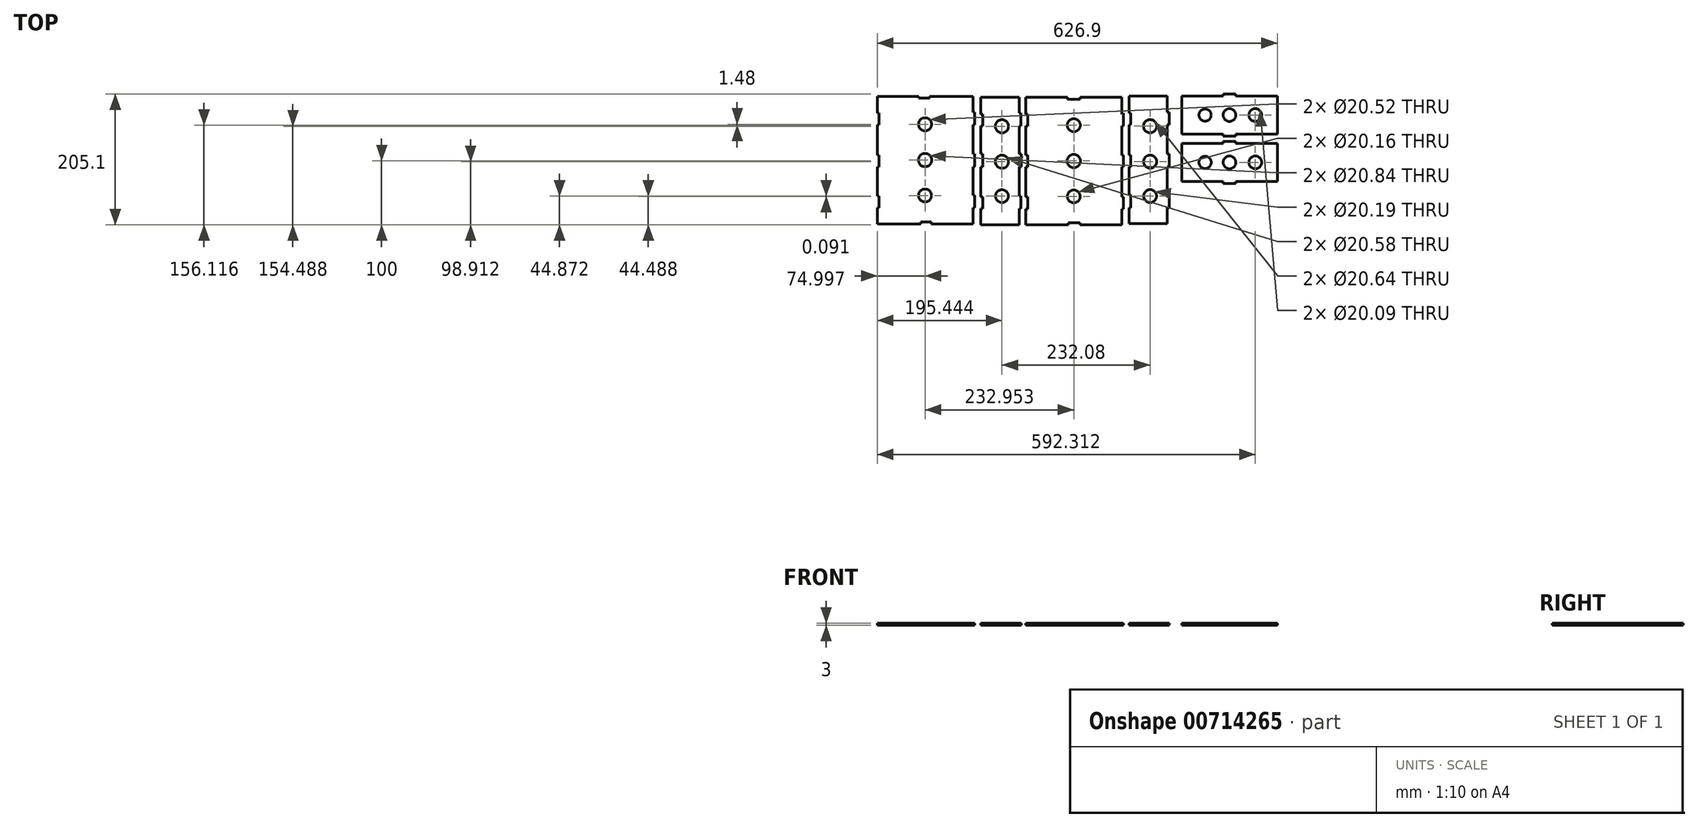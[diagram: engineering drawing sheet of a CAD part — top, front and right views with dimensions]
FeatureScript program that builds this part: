
annotation { "Feature Type Name" : "Feature", "Feature Type Description" : "" }
export const myFeature = defineFeature(function(context is Context, id is Id, definition is map)
    precondition{}
    {
        {
            var Q0;
            Q0=qCreatedBy(makeId("Top.planeOp"),FACE);
            var sketch = newSketch(context, id + "F0", { "sketchPlane" : qUnion([Q0])});
            skLineSegment(sketch, "E0.bottom", {"start": v(75, -100) * mm, "end": v(10, -100) * mm});
            skLineSegment(sketch, "E0.top", {"start": v(75, 100) * mm, "end": v(10, 100) * mm});
            skLineSegment(sketch, "E0.left", {"start": v(75, -100) * mm, "end": v(75, -75) * mm});
            skLineSegment(sketch, "E0.right", {"start": v(-75, -100) * mm, "end": v(-75, -75) * mm});
            skLineSegment(sketch, "E1", {"start": v(-75, 73.5) * mm, "end": v(-72, 73.5) * mm});
            skLineSegment(sketch, "E2", {"start": v(-72, 73.5) * mm, "end": v(-72, 55) * mm});
            skLineSegment(sketch, "E3", {"start": v(-75, 55) * mm, "end": v(-72, 55) * mm});
            skLineSegment(sketch, "E4", {"start": v(-75, -56.5) * mm, "end": v(-72, -56.5) * mm});
            skLineSegment(sketch, "E5", {"start": v(-72, -56.5) * mm, "end": v(-72, -75) * mm});
            skLineSegment(sketch, "E6", {"start": v(-72, -75) * mm, "end": v(-75, -75) * mm});
            skLineSegment(sketch, "E7.trimOffspring", {"start": v(-75, 73.5) * mm, "end": v(-75, 100) * mm});
            skLineSegment(sketch, "E8.trimOffspring", {"start": v(-75, -56.5) * mm, "end": v(-75, -9.04) * mm});
            skLineSegment(sketch, "E9.trimOffspring", {"start": v(75, 73.5) * mm, "end": v(75, 100) * mm});
            skLineSegment(sketch, "E10.trimOffspring", {"start": v(75, -56.5) * mm, "end": v(75, -9.04) * mm});
            skLineSegment(sketch, "E11.MirrorCS", {"start": v(75, -56.5) * mm, "end": v(78, -56.5) * mm});
            skLineSegment(sketch, "E12.MirrorCS", {"start": v(78, -75) * mm, "end": v(75, -75) * mm});
            skLineSegment(sketch, "E13.MirrorCS", {"start": v(75, 55) * mm, "end": v(78, 55) * mm});
            skLineSegment(sketch, "E14.MirrorCS", {"start": v(75, 73.5) * mm, "end": v(77.6, 75) * mm});
            skLineSegment(sketch, "E15.bottom", {"start": v(-85.64, -99.9) * mm, "end": v(-145.64, -99.9) * mm});
            skLineSegment(sketch, "E15.top", {"start": v(-85.64, 100.1) * mm, "end": v(-145.64, 100.1) * mm});
            skLineSegment(sketch, "E15.left", {"start": v(-85.64, -99.9) * mm, "end": v(-85.64, -74.9) * mm});
            skLineSegment(sketch, "E15.right", {"start": v(-145.64, -99.9) * mm, "end": v(-145.64, -74.9) * mm});
            skLineSegment(sketch, "E16", {"start": v(-145.64, 73.6) * mm, "end": v(-142.64, 73.6) * mm});
            skLineSegment(sketch, "E17", {"start": v(-142.64, 73.6) * mm, "end": v(-142.64, 55.1) * mm});
            skLineSegment(sketch, "E18", {"start": v(-145.64, 55.1) * mm, "end": v(-142.64, 55.1) * mm});
            skLineSegment(sketch, "E19", {"start": v(-145.64, -56.4) * mm, "end": v(-142.64, -56.4) * mm});
            skLineSegment(sketch, "E20", {"start": v(-142.64, -56.4) * mm, "end": v(-142.64, -74.9) * mm});
            skLineSegment(sketch, "E21", {"start": v(-142.64, -74.9) * mm, "end": v(-145.64, -74.9) * mm});
            skLineSegment(sketch, "E22.trimOffspring", {"start": v(-145.64, 73.6) * mm, "end": v(-145.64, 100.1) * mm});
            skLineSegment(sketch, "E23.trimOffspring", {"start": v(-145.64, -56.4) * mm, "end": v(-145.64, -9.04) * mm});
            skLineSegment(sketch, "E24.trimOffspring", {"start": v(-85.64, 75.1) * mm, "end": v(-85.64, 100.1) * mm});
            skLineSegment(sketch, "E25.trimOffspring", {"start": v(-85.64, -54.9) * mm, "end": v(-85.64, -9.04) * mm});
            skLineSegment(sketch, "E26.MirrorCS", {"start": v(-85.64, -54.9) * mm, "end": v(-82.64, -54.9) * mm});
            skLineSegment(sketch, "E27.MirrorCS", {"start": v(-82.64, -74.9) * mm, "end": v(-85.64, -74.9) * mm});
            skLineSegment(sketch, "E28.MirrorCS", {"start": v(-85.64, 55.1) * mm, "end": v(-82.64, 55.1) * mm});
            skLineSegment(sketch, "E29.MirrorCS", {"start": v(-85.64, 75.1) * mm, "end": v(-82.64, 75.1) * mm});
            skLineSegment(sketch, "E30", {"start": v(-82.64, 75.1) * mm, "end": v(-82.64, 55.1) * mm});
            skLineSegment(sketch, "E31", {"start": v(-82.64, -54.9) * mm, "end": v(-82.64, -74.9) * mm});
            skLineSegment(sketch, "E32.bottom", {"start": v(10, -97) * mm, "end": v(-8.5, -97) * mm});
            skLineSegment(sketch, "E32.left", {"start": v(10, -97) * mm, "end": v(10, -100) * mm});
            skLineSegment(sketch, "E32.right", {"start": v(-8.5, -97) * mm, "end": v(-8.5, -100) * mm});
            skLineSegment(sketch, "E33.MirrorCS", {"start": v(10, 97) * mm, "end": v(10, 100) * mm});
            skLineSegment(sketch, "E34.MirrorCS", {"start": v(-10, 97) * mm, "end": v(-10, 100) * mm});
            skLineSegment(sketch, "E35.trimOffspring", {"start": v(-10, 100) * mm, "end": v(-75, 100) * mm});
            skLineSegment(sketch, "E36.trimOffspring", {"start": v(-8.5, -100) * mm, "end": v(-75, -100) * mm});
            skCircle(sketch, "E37", {"center": v(0, 56.12) * mm, "radius": 10.26 * mm});
            skCircle(sketch, "E38", {"center": v(0, -55.51) * mm, "radius": 10.08 * mm});
            skCircle(sketch, "E39", {"center": v(0, 0) * mm, "radius": 10.42 * mm});
            skPoint(sketch, "E40.middle", {"position": v(-112.5, -1.09) * mm});
            skCircle(sketch, "E41", {"center": v(-112.5, -55.13) * mm, "radius": 10.1 * mm});
            skCircle(sketch, "E42", {"center": v(-112.5, -1.09) * mm, "radius": 10.3 * mm});
            skCircle(sketch, "E43", {"center": v(-112.5, 54.49) * mm, "radius": 10.32 * mm});
            skLineSegment(sketch, "E44", {"start": v(-10, 97) * mm, "end": v(10, 97) * mm});
            skLineSegment(sketch, "E45", {"start": v(77.6, 75) * mm, "end": v(78, 55) * mm});
            skLineSegment(sketch, "E46", {"start": v(78, -56.5) * mm, "end": v(78, -75) * mm});
            skLineSegment(sketch, "E47.bottom", {"start": v(146.44, -98.31) * mm, "end": v(86.44, -98.31) * mm});
            skLineSegment(sketch, "E47.top", {"start": v(146.44, 101.69) * mm, "end": v(86.44, 101.69) * mm});
            skLineSegment(sketch, "E47.left", {"start": v(146.44, -98.31) * mm, "end": v(146.44, -73.31) * mm});
            skLineSegment(sketch, "E47.right", {"start": v(86.44, -98.31) * mm, "end": v(86.44, -73.31) * mm});
            skLineSegment(sketch, "E48", {"start": v(86.44, 75.19) * mm, "end": v(89.44, 75.19) * mm});
            skLineSegment(sketch, "E49", {"start": v(89.44, 75.19) * mm, "end": v(89.44, 56.69) * mm});
            skLineSegment(sketch, "E50", {"start": v(86.44, 56.69) * mm, "end": v(89.44, 56.69) * mm});
            skLineSegment(sketch, "E51", {"start": v(86.44, -53.31) * mm, "end": v(89.44, -53.31) * mm});
            skLineSegment(sketch, "E52", {"start": v(89.44, -53.31) * mm, "end": v(89.44, -73.31) * mm});
            skLineSegment(sketch, "E53", {"start": v(89.44, -73.31) * mm, "end": v(86.44, -73.31) * mm});
            skLineSegment(sketch, "E54.trimOffspring", {"start": v(86.44, 75.19) * mm, "end": v(86.44, 101.69) * mm});
            skLineSegment(sketch, "E55.trimOffspring", {"start": v(86.44, -53.31) * mm, "end": v(86.44, -9.04) * mm});
            skLineSegment(sketch, "E56.trimOffspring", {"start": v(146.44, 76.69) * mm, "end": v(146.44, 101.69) * mm});
            skLineSegment(sketch, "E57.trimOffspring", {"start": v(146.44, -53.31) * mm, "end": v(146.44, -9.04) * mm});
            skLineSegment(sketch, "E58.MirrorCS", {"start": v(146.44, -53.31) * mm, "end": v(149.44, -53.31) * mm});
            skLineSegment(sketch, "E59.MirrorCS", {"start": v(149.44, -73.31) * mm, "end": v(146.44, -73.31) * mm});
            skLineSegment(sketch, "E60.MirrorCS", {"start": v(146.44, 56.69) * mm, "end": v(149.44, 56.69) * mm});
            skLineSegment(sketch, "E61.MirrorCS", {"start": v(146.44, 76.69) * mm, "end": v(149.44, 76.69) * mm});
            skLineSegment(sketch, "E62", {"start": v(149.44, 76.69) * mm, "end": v(149.44, 56.69) * mm});
            skLineSegment(sketch, "E63", {"start": v(149.44, -53.31) * mm, "end": v(149.44, -73.31) * mm});
            skPoint(sketch, "E64.middle", {"position": v(119.57, -1) * mm});
            skCircle(sketch, "E65", {"center": v(119.57, -55.04) * mm, "radius": 10.1 * mm});
            skCircle(sketch, "E66", {"center": v(119.57, -1) * mm, "radius": 10.3 * mm});
            skCircle(sketch, "E67", {"center": v(119.57, 54.58) * mm, "radius": 10.32 * mm});
            skLineSegment(sketch, "E68.bottom", {"start": v(-157.95, -98.52) * mm, "end": v(-222.95, -98.52) * mm});
            skLineSegment(sketch, "E68.top", {"start": v(-157.95, 101.48) * mm, "end": v(-225.53, 101.48) * mm});
            skLineSegment(sketch, "E68.left", {"start": v(-157.95, -98.52) * mm, "end": v(-157.95, -73.52) * mm});
            skLineSegment(sketch, "E68.right", {"start": v(-307.95, -98.52) * mm, "end": v(-307.95, -73.52) * mm});
            skLineSegment(sketch, "E69", {"start": v(-307.95, 74.98) * mm, "end": v(-304.95, 74.98) * mm});
            skLineSegment(sketch, "E70", {"start": v(-304.95, 74.98) * mm, "end": v(-304.95, 56.48) * mm});
            skLineSegment(sketch, "E71", {"start": v(-307.95, 56.48) * mm, "end": v(-304.95, 56.48) * mm});
            skLineSegment(sketch, "E72", {"start": v(-307.95, -55.02) * mm, "end": v(-304.95, -55.02) * mm});
            skLineSegment(sketch, "E73", {"start": v(-304.95, -55.02) * mm, "end": v(-304.95, -73.52) * mm});
            skLineSegment(sketch, "E74", {"start": v(-304.95, -73.52) * mm, "end": v(-307.95, -73.52) * mm});
            skLineSegment(sketch, "E75.trimOffspring", {"start": v(-307.95, 74.98) * mm, "end": v(-307.95, 101.48) * mm});
            skLineSegment(sketch, "E76.trimOffspring", {"start": v(-307.95, -55.02) * mm, "end": v(-307.95, -9.04) * mm});
            skLineSegment(sketch, "E77.trimOffspring", {"start": v(-157.95, 76.48) * mm, "end": v(-157.95, 101.48) * mm});
            skLineSegment(sketch, "E78.trimOffspring", {"start": v(-157.95, -53.52) * mm, "end": v(-157.95, -9.04) * mm});
            skLineSegment(sketch, "E79.MirrorCS", {"start": v(-157.95, -53.52) * mm, "end": v(-154.95, -53.52) * mm});
            skLineSegment(sketch, "E80.MirrorCS", {"start": v(-154.95, -73.52) * mm, "end": v(-157.95, -73.52) * mm});
            skLineSegment(sketch, "E81.MirrorCS", {"start": v(-157.95, 56.48) * mm, "end": v(-154.95, 56.48) * mm});
            skLineSegment(sketch, "E82.MirrorCS", {"start": v(-157.95, 76.48) * mm, "end": v(-154.95, 76.48) * mm});
            skLineSegment(sketch, "E83.bottom", {"start": v(-222.95, -95.52) * mm, "end": v(-239.95, -95.52) * mm});
            skLineSegment(sketch, "E83.left", {"start": v(-222.95, -95.52) * mm, "end": v(-222.95, -98.52) * mm});
            skLineSegment(sketch, "E83.right", {"start": v(-239.95, -95.52) * mm, "end": v(-239.95, -98.52) * mm});
            skLineSegment(sketch, "E84.MirrorCS", {"start": v(-225.88, 98.5) * mm, "end": v(-225.53, 101.48) * mm});
            skLineSegment(sketch, "E85.MirrorCS", {"start": v(-242.88, 98.48) * mm, "end": v(-242.96, 101.48) * mm});
            skLineSegment(sketch, "E86.trimOffspring", {"start": v(-242.96, 101.48) * mm, "end": v(-307.95, 101.48) * mm});
            skLineSegment(sketch, "E87.trimOffspring", {"start": v(-239.95, -98.52) * mm, "end": v(-307.95, -98.52) * mm});
            skCircle(sketch, "E88", {"center": v(-232.95, 57.6) * mm, "radius": 10.26 * mm});
            skCircle(sketch, "E89", {"center": v(-232.95, -54.03) * mm, "radius": 10.08 * mm});
            skCircle(sketch, "E90", {"center": v(-232.95, 1.48) * mm, "radius": 10.42 * mm});
            skLineSegment(sketch, "E91", {"start": v(-242.88, 98.48) * mm, "end": v(-225.88, 98.5) * mm});
            skLineSegment(sketch, "E92", {"start": v(-154.95, 76.48) * mm, "end": v(-154.95, 56.48) * mm});
            skLineSegment(sketch, "E93", {"start": v(-154.95, -53.52) * mm, "end": v(-154.95, -73.52) * mm});
            skLineSegment(sketch, "E94.bottom", {"start": v(168.91, 42.1) * mm, "end": v(233.91, 42.1) * mm});
            skLineSegment(sketch, "E94.top", {"start": v(168.91, 102.1) * mm, "end": v(233.91, 102.1) * mm});
            skLineSegment(sketch, "E94.left", {"start": v(168.91, 42.1) * mm, "end": v(168.91, 102.1) * mm});
            skLineSegment(sketch, "E94.right", {"start": v(318.91, 42.1) * mm, "end": v(318.91, 102.1) * mm});
            skLineSegment(sketch, "E95.bottom", {"start": v(233.91, 105.1) * mm, "end": v(253.91, 105.1) * mm});
            skLineSegment(sketch, "E95.left", {"start": v(233.91, 105.1) * mm, "end": v(233.91, 102.1) * mm});
            skLineSegment(sketch, "E95.right", {"start": v(253.91, 105.1) * mm, "end": v(253.91, 102.1) * mm});
            skLineSegment(sketch, "E96.MirrorCS", {"start": v(253.91, 39.1) * mm, "end": v(253.91, 42.1) * mm});
            skLineSegment(sketch, "E97.MirrorCS", {"start": v(233.91, 39.1) * mm, "end": v(233.91, 42.1) * mm});
            skLineSegment(sketch, "E98.trimOffspring", {"start": v(253.91, 102.1) * mm, "end": v(318.91, 102.1) * mm});
            skLineSegment(sketch, "E99.trimOffspring", {"start": v(253.91, 42.1) * mm, "end": v(318.91, 42.1) * mm});
            skCircle(sketch, "E100", {"center": v(205.7, 72.1) * mm, "radius": 9.62 * mm});
            skCircle(sketch, "E101", {"center": v(243.91, 72.1) * mm, "radius": 10 * mm});
            skCircle(sketch, "E102", {"center": v(284.36, 72.1) * mm, "radius": 10.05 * mm});
            skLineSegment(sketch, "E103", {"start": v(233.91, 39.1) * mm, "end": v(253.91, 39.1) * mm});
            skLineSegment(sketch, "E104.bottom", {"start": v(168.95, -32.17) * mm, "end": v(233.95, -32.17) * mm});
            skLineSegment(sketch, "E104.top", {"start": v(168.95, 27.83) * mm, "end": v(233.95, 27.83) * mm});
            skLineSegment(sketch, "E104.left", {"start": v(168.95, -32.17) * mm, "end": v(168.95, 27.83) * mm});
            skLineSegment(sketch, "E104.right", {"start": v(318.95, -32.17) * mm, "end": v(318.95, 27.83) * mm});
            skLineSegment(sketch, "E105.bottom", {"start": v(233.95, 30.83) * mm, "end": v(253.95, 30.83) * mm});
            skLineSegment(sketch, "E105.left", {"start": v(233.95, 30.83) * mm, "end": v(233.95, 27.83) * mm});
            skLineSegment(sketch, "E105.right", {"start": v(253.95, 30.83) * mm, "end": v(253.95, 27.83) * mm});
            skLineSegment(sketch, "E106.MirrorCS", {"start": v(253.95, -35.17) * mm, "end": v(253.95, -32.17) * mm});
            skLineSegment(sketch, "E107.MirrorCS", {"start": v(233.95, -35.17) * mm, "end": v(233.95, -32.17) * mm});
            skLineSegment(sketch, "E108.trimOffspring", {"start": v(253.95, 27.83) * mm, "end": v(318.95, 27.83) * mm});
            skLineSegment(sketch, "E109.trimOffspring", {"start": v(253.95, -32.17) * mm, "end": v(318.95, -32.17) * mm});
            skCircle(sketch, "E110", {"center": v(205.74, -2.17) * mm, "radius": 9.62 * mm});
            skCircle(sketch, "E111", {"center": v(243.95, -2.17) * mm, "radius": 10 * mm});
            skCircle(sketch, "E112", {"center": v(284.4, -2.17) * mm, "radius": 10.05 * mm});
            skLineSegment(sketch, "E113", {"start": v(233.95, -35.17) * mm, "end": v(253.95, -35.17) * mm});
            skLineSegment(sketch, "E114.bottom", {"start": v(-304.95, -9.04) * mm, "end": v(-307.95, -9.04) * mm});
            skLineSegment(sketch, "E114.top", {"start": v(-304.95, 9.46) * mm, "end": v(-307.95, 9.46) * mm});
            skLineSegment(sketch, "E114.left", {"start": v(-304.95, -9.04) * mm, "end": v(-304.95, 9.46) * mm});
            skLineSegment(sketch, "E115.trimOffspring", {"start": v(-307.95, 9.46) * mm, "end": v(-307.95, 56.48) * mm});
            skLineSegment(sketch, "E116.MirrorCS", {"start": v(-154.95, 10.96) * mm, "end": v(-157.95, 10.96) * mm});
            skLineSegment(sketch, "E117.MirrorCS", {"start": v(-154.95, -9.04) * mm, "end": v(-154.95, 10.96) * mm});
            skLineSegment(sketch, "E118.MirrorCS", {"start": v(-154.95, -9.04) * mm, "end": v(-157.95, -9.04) * mm});
            skLineSegment(sketch, "E119.trimOffspring", {"start": v(-157.95, 10.96) * mm, "end": v(-157.95, 56.48) * mm});
            skPoint(sketch, "E120", {"position": v(-145.64, 10.96) * mm});
            skPoint(sketch, "E121", {"position": v(-145.64, -9.04) * mm});
            skLineSegment(sketch, "E122", {"start": v(-145.64, 10.96) * mm, "end": v(-142.64, 10.96) * mm});
            skLineSegment(sketch, "E123", {"start": v(-142.64, 10.96) * mm, "end": v(-142.64, -9.04) * mm});
            skLineSegment(sketch, "E124", {"start": v(-142.64, -9.04) * mm, "end": v(-145.64, -9.04) * mm});
            skLineSegment(sketch, "E125.trimOffspring", {"start": v(-145.64, 10.96) * mm, "end": v(-145.64, 55.1) * mm});
            skLineSegment(sketch, "E126.MirrorCS", {"start": v(-82.37, 10.96) * mm, "end": v(-82.37, -9.04) * mm});
            skLineSegment(sketch, "E127", {"start": v(-85.64, 10.96) * mm, "end": v(-82.37, 10.96) * mm});
            skLineSegment(sketch, "E128", {"start": v(-85.64, -9.04) * mm, "end": v(-82.37, -9.04) * mm});
            skLineSegment(sketch, "E129.trimOffspring", {"start": v(-85.64, 10.96) * mm, "end": v(-85.64, 55.1) * mm});
            skLineSegment(sketch, "E130", {"start": v(-75, 9.46) * mm, "end": v(-72, 9.46) * mm});
            skLineSegment(sketch, "E131", {"start": v(-72, 9.46) * mm, "end": v(-72, -9.04) * mm});
            skLineSegment(sketch, "E132", {"start": v(-72, -9.04) * mm, "end": v(-75, -9.04) * mm});
            skLineSegment(sketch, "E133.trimOffspring", {"start": v(-75, 9.46) * mm, "end": v(-75, 55) * mm});
            skLineSegment(sketch, "E134", {"start": v(75, 9.46) * mm, "end": v(78, 9.46) * mm});
            skLineSegment(sketch, "E135", {"start": v(78, 9.46) * mm, "end": v(78, -9.04) * mm});
            skLineSegment(sketch, "E136", {"start": v(78, -9.04) * mm, "end": v(75, -9.04) * mm});
            skLineSegment(sketch, "E137.trimOffspring", {"start": v(75, 9.46) * mm, "end": v(75, 55) * mm});
            skLineSegment(sketch, "E138", {"start": v(86.44, 9.46) * mm, "end": v(89.44, 9.46) * mm});
            skLineSegment(sketch, "E139", {"start": v(89.44, 9.46) * mm, "end": v(89.44, -9.04) * mm});
            skLineSegment(sketch, "E140", {"start": v(89.44, -9.04) * mm, "end": v(86.44, -9.04) * mm});
            skLineSegment(sketch, "E141.trimOffspring", {"start": v(86.44, 9.46) * mm, "end": v(86.44, 56.69) * mm});
            skLineSegment(sketch, "E142", {"start": v(146.44, 10.96) * mm, "end": v(149.44, 10.96) * mm});
            skLineSegment(sketch, "E143", {"start": v(149.44, 10.96) * mm, "end": v(149.44, -9.04) * mm});
            skLineSegment(sketch, "E144", {"start": v(149.44, -9.04) * mm, "end": v(146.44, -9.04) * mm});
            skLineSegment(sketch, "E145.trimOffspring", {"start": v(146.44, 10.96) * mm, "end": v(146.44, 56.69) * mm});
            skSolve(sketch);
        }
        {
            var Q0;
            Q0 = qSketchRegion(id + "F0", true);
            extrude(context, id + "F1", {"entities" : qUnion([Q0]), "depth" : 3 * mm, "offsetDistance" : 25 * mm});
        }
    });
